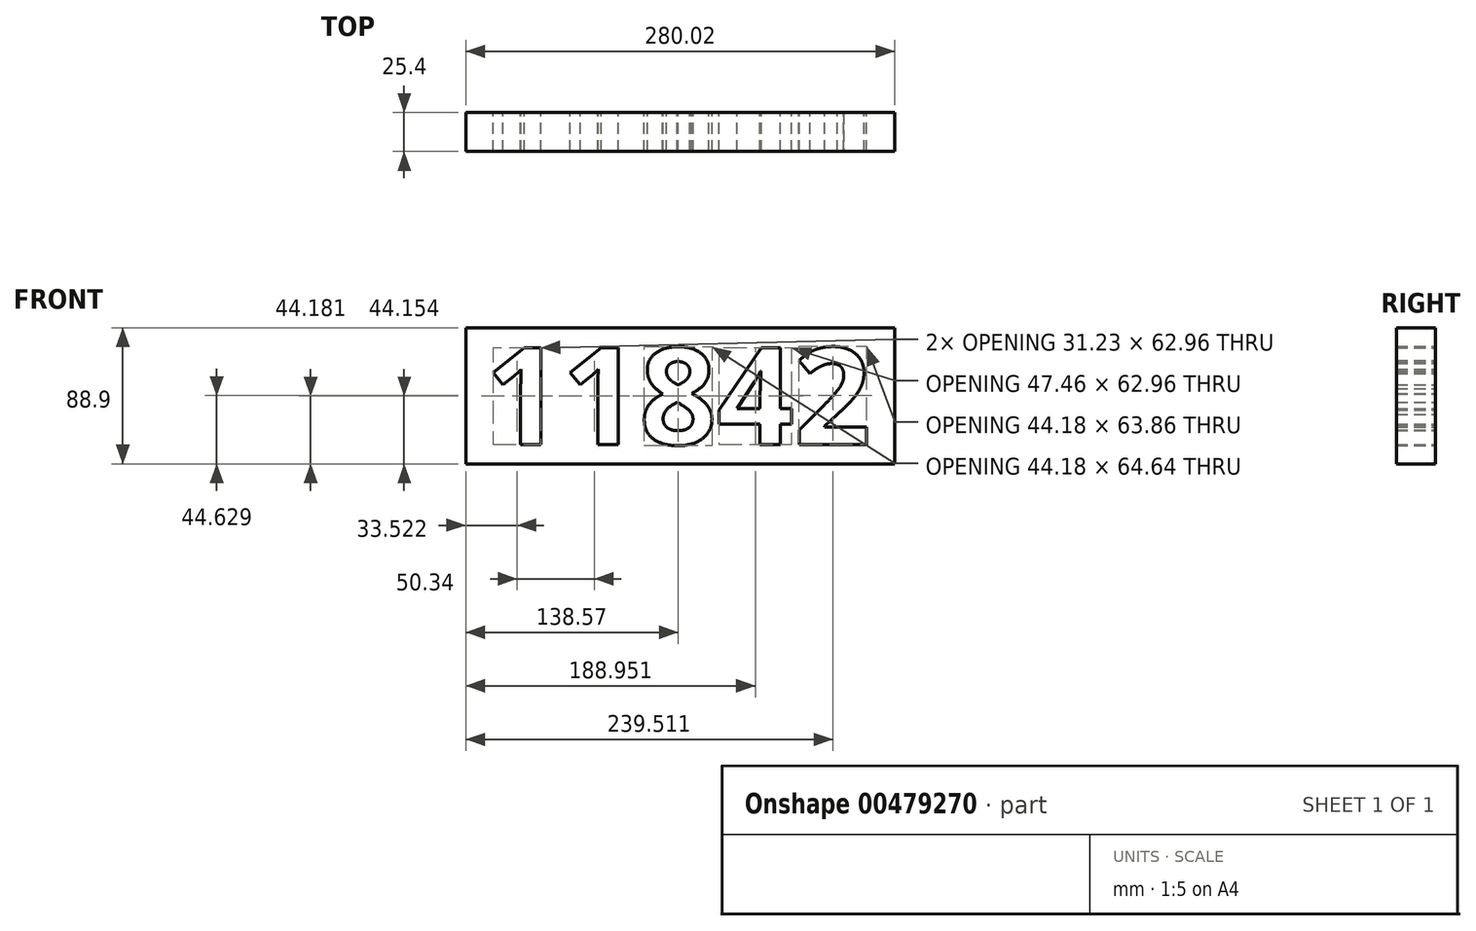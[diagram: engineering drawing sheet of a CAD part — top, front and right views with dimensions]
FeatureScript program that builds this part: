
annotation { "Feature Type Name" : "Feature", "Feature Type Description" : "" }
export const myFeature = defineFeature(function(context is Context, id is Id, definition is map)
    precondition{}
    {
        {
            var Q0;
            Q0=qCreatedBy(makeId("Front.planeOp"),FACE);
            var sketch = newSketch(context, id + "F0", { "sketchPlane" : qUnion([Q0])});
            skLineSegment(sketch, "E0.bottom", {"start": v(0, 0) * mm, "end": v(280.02, 0) * mm});
            skLineSegment(sketch, "E0.top", {"start": v(0, 88.9) * mm, "end": v(280.02, 88.9) * mm});
            skLineSegment(sketch, "E0.left", {"start": v(0, 0) * mm, "end": v(0, 88.9) * mm});
            skLineSegment(sketch, "E0.right", {"start": v(280.02, 0) * mm, "end": v(280.02, 88.9) * mm});
            skLineSegment(sketch, "E1.bottom", {"start": v(0, 88.9) * mm, "end": v(12.7, 88.9) * mm, "construction": true});
            skLineSegment(sketch, "E1.top", {"start": v(0, 76.2) * mm, "end": v(12.7, 76.2) * mm, "construction": true});
            skLineSegment(sketch, "E1.left", {"start": v(0, 88.9) * mm, "end": v(0, 76.2) * mm, "construction": true});
            skLineSegment(sketch, "E1.right", {"start": v(12.7, 88.9) * mm, "end": v(12.7, 76.2) * mm, "construction": true});
            skLineSegment(sketch, "E2.bottom", {"start": v(280.02, 0) * mm, "end": v(267.32, 0) * mm, "construction": true});
            skLineSegment(sketch, "E2.top", {"start": v(280.02, 12.7) * mm, "end": v(267.32, 12.7) * mm, "construction": true});
            skLineSegment(sketch, "E2.left", {"start": v(280.02, 0) * mm, "end": v(280.02, 12.7) * mm, "construction": true});
            skLineSegment(sketch, "E2.right", {"start": v(267.32, 0) * mm, "end": v(267.32, 12.7) * mm, "construction": true});
            skText(sketch, "E3", { "text": "11842", "fontName": "OpenSans-Bold.ttf"});
            const initialGuessF0  = {"E3": [0.0127, 0.0127, 1, 0, 0.0635]};
            skSetInitialGuess(sketch, initialGuessF0);
            skSolve(sketch);
        }
        {
            var Q0;
            Q0=makeQuery(id+"F0.imprint","IMPRINT",FACE,{"disambiguationData":[TD([[makeQuery(id+"F0.imprint","IMPRINT",EDGE,{"derivedFrom":sQuery(id+"F0.wireOp",EDGE,"E0.bottom")}),1.0]])]});
            var Q1;
            Q1=makeQuery(id+"F0.imprint","IMPRINT",FACE,{"disambiguationData":[TD([[makeQuery(id+"F0.imprint","IMPRINT",EDGE,{"derivedFrom":sQuery(id+"F0.wireOp",EDGE,"E3.sketch_text.stroke-62")}),1.0]])]});
            var Q2;
            Q2=makeQuery(id+"F0.imprint","IMPRINT",FACE,{"disambiguationData":[TD([[makeQuery(id+"F0.imprint","IMPRINT",EDGE,{"derivedFrom":sQuery(id+"F0.wireOp",EDGE,"E3.sketch_text.stroke-36")}),1.0]])]});
            var Q3;
            Q3=makeQuery(id+"F0.imprint","IMPRINT",FACE,{"disambiguationData":[TD([[makeQuery(id+"F0.imprint","IMPRINT",EDGE,{"derivedFrom":sQuery(id+"F0.wireOp",EDGE,"E3.sketch_text.stroke-43")}),1.0]])]});
            extrude(context, id + "F1", {"entities" : qUnion([Q0, Q1, Q2, Q3]), "depth" : 25.4 * mm});
        }
    });
